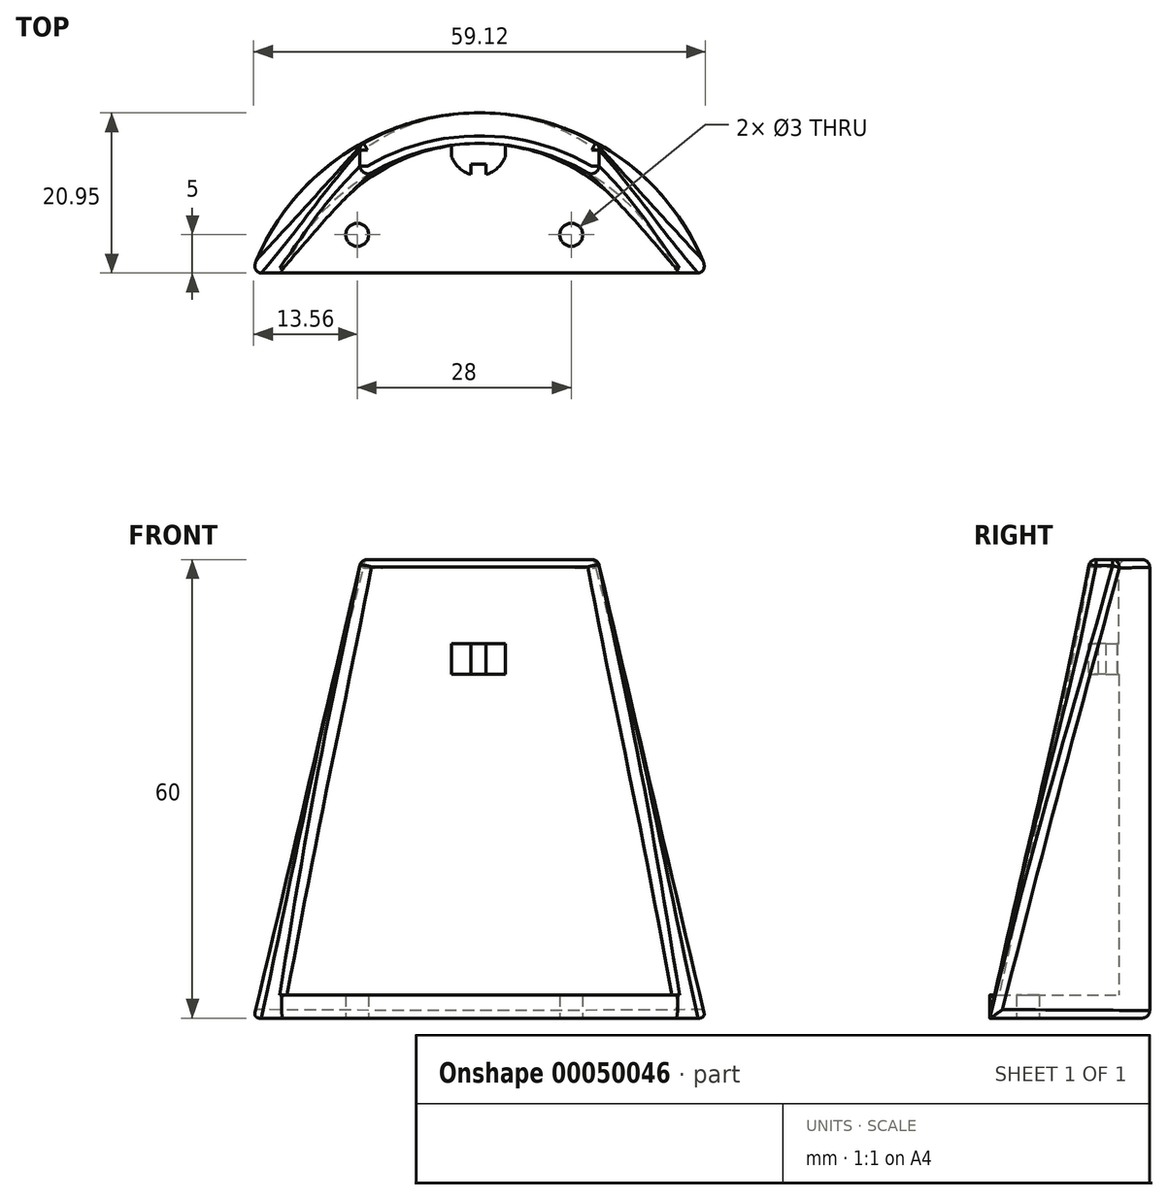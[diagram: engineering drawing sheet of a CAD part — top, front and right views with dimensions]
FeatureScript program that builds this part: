
annotation { "Feature Type Name" : "Feature", "Feature Type Description" : "" }
export const myFeature = defineFeature(function(context is Context, id is Id, definition is map)
    precondition{}
    {
        {
            var Q0;
            Q0=qCreatedBy(makeId("Top.planeOp"),FACE);
            var sketch = newSketch(context, id + "F0", { "sketchPlane" : qUnion([Q0])});
            skLineSegment(sketch, "E0.bottom", {"start": v(-24.17, 9.79) * mm, "end": v(35.83, 9.79) * mm, "construction": true});
            skLineSegment(sketch, "E0.top", {"start": v(-24.17, -15.21) * mm, "end": v(-20.17, -15.21) * mm});
            skLineSegment(sketch, "E0.left", {"start": v(-24.17, 9.79) * mm, "end": v(-24.17, -15.21) * mm, "construction": true});
            skLineSegment(sketch, "E0.right", {"start": v(35.83, 9.79) * mm, "end": v(35.83, -15.21) * mm, "construction": true});
            skArc(sketch, "E1", {"start": v(35.83, -15.21) * mm, "mid": v(5.83, 5.74) * mm, "end": v(-24.17, -15.21) * mm});
            skArc(sketch, "E2", {"start": v(31.83, -15.21) * mm, "mid": v(5.83, 1.74) * mm, "end": v(-20.17, -15.21) * mm});
            skLineSegment(sketch, "E3.trimOffspring", {"start": v(31.83, -15.21) * mm, "end": v(35.83, -15.21) * mm});
            skLineSegment(sketch, "E4", {"start": v(-20.17, -15.21) * mm, "end": v(31.83, -15.21) * mm});
            skCircle(sketch, "E5", {"center": v(-10.17, -10.21) * mm, "radius": 1.5 * mm});
            skCircle(sketch, "E6", {"center": v(17.83, -10.21) * mm, "radius": 1.5 * mm});
            skSolve(sketch);
        }
        {
            var Q0;
            Q0=qCreatedBy(makeId("Top.planeOp"),FACE);
            cPlane(context, id + "F1", {"entities" : qUnion([Q0]), "cplaneType" : CPlaneType.OFFSET, "offset" : 60 * mm, "width" : 150 * mm, "height" : 150 * mm});
        }
        {
            var Q0;
            Q0=qCreatedBy(id+"F1.planeOp",FACE);
            var sketch = newSketch(context, id + "F2", { "sketchPlane" : qUnion([Q0])});
            skArc(sketch, "E7", {"start": v(21.31, -2.84) * mm, "mid": v(5.83, 1.74) * mm, "end": v(-9.65, -2.84) * mm});
            skArc(sketch, "E8", {"start": v(21.31, 1.74) * mm, "mid": v(5.83, 5.74) * mm, "end": v(-9.65, 1.74) * mm});
            skPoint(sketch, "E8.startSnap0", {"position": v(5.83, 1.74) * mm});
            skPoint(sketch, "E8.endSnap0", {"position": v(5.83, 1.74) * mm});
            skLineSegment(sketch, "E9", {"start": v(-9.65, 1.74) * mm, "end": v(-9.65, -2.84) * mm});
            skLineSegment(sketch, "E10", {"start": v(21.31, 1.74) * mm, "end": v(21.31, -2.84) * mm});
            skSolve(sketch);
        }
        {
            var Q0;
            Q0=makeQuery(id+"F0.imprint","IMPRINT",FACE,{"disambiguationData":[TD([[makeQuery(id+"F0.imprint","IMPRINT",EDGE,{"derivedFrom":sQuery(id+"F0.wireOp",EDGE,"E0.top")}),1.0]])]});
            var Q1;
            Q1=makeQuery(id+"F2.imprint","IMPRINT",FACE,{"disambiguationData":[TD([[makeQuery(id+"F2.imprint","IMPRINT",EDGE,{"derivedFrom":sQuery(id+"F2.wireOp",EDGE,"E7")}),-1.0]])]});
            loft(context, id + "F3", {"sheetProfilesArray" : [{ "sheetProfileEntities" : qUnion([Q0]) }, { "sheetProfileEntities" : qUnion([Q1]) }]});
        }
        {
            var Q0;
            Q0=makeQuery(id+"F0.imprint","IMPRINT",FACE,{"disambiguationData":[TD([[makeQuery(id+"F0.imprint","IMPRINT",EDGE,{"derivedFrom":sQuery(id+"F0.wireOp",EDGE,"E2")}),1.0]])]});
            extrude(context, id + "F4", {"entities" : qUnion([Q0]), "operationType" : NewBodyOperationType.ADD, "depth" : 3 * mm});
        }
        {
            var Q0;
            Q0=makeQuery(id+"F4.opExtrude","SWEPT_EDGE",EDGE,{"disambiguationData":[OSD([sQuery(id+"F0.wireOp",EDGE,"E0.top"),sQuery(id+"F0.wireOp",EDGE,"E2"),sQuery(id+"F0.wireOp",EDGE,"E4")])]});
            var Q1;
            Q1=makeQuery(id+"F4.opExtrude","SWEPT_EDGE",EDGE,{"disambiguationData":[OSD([sQuery(id+"F0.wireOp",EDGE,"E2"),sQuery(id+"F0.wireOp",EDGE,"E3.trimOffspring"),sQuery(id+"F0.wireOp",EDGE,"E4")])]});
            var Q2;
            {var subQ0=sQuery(id+"F0.wireOp",EDGE,"E2");var subQ1=sQuery(id+"F0.wireOp",EDGE,"E4");Q2=makeQuery(id+"F4.boolean.opBoolean","SPLIT",EDGE,{"disambiguationData":[TD([makeQuery(id+"F3.opLoft","SWEPT_FACE",FACE,{"disambiguationData":[OSD([sQuery(id+"F0.wireOp",EDGE,"E1"),subQ0,sQuery(id+"F0.wireOp",EDGE,"E3.trimOffspring"),subQ1,sQuery(id+"F2.wireOp",EDGE,"E7"),sQuery(id+"F2.wireOp",EDGE,"E8"),sQuery(id+"F2.wireOp",EDGE,"E10")])]})])],"derivedFrom":makeQuery(id+"F4.opExtrude","CAP_EDGE",EDGE,{"disambiguationData":[OSD([subQ0])],"isStart":false})});}
            var Q3;
            {var subQ0=sQuery(id+"F0.wireOp",EDGE,"E2");var subQ1=sQuery(id+"F0.wireOp",EDGE,"E4");Q3=makeQuery(id+"F4.boolean.opBoolean","SPLIT",EDGE,{"disambiguationData":[TD([makeQuery(id+"F3.opLoft","SWEPT_FACE",FACE,{"disambiguationData":[OSD([sQuery(id+"F0.wireOp",EDGE,"E0.top"),sQuery(id+"F0.wireOp",EDGE,"E1"),subQ0,subQ1,sQuery(id+"F2.wireOp",EDGE,"E7"),sQuery(id+"F2.wireOp",EDGE,"E8"),sQuery(id+"F2.wireOp",EDGE,"E9")])]})])],"derivedFrom":makeQuery(id+"F4.opExtrude","CAP_EDGE",EDGE,{"disambiguationData":[OSD([subQ0])],"isStart":false})});}
            fillet(context, id + "F5", {"entities" : qUnion([Q0, Q1, Q2, Q3]), "radius" : .2 * mm, "tangentPropagation" : true, "allowEdgeOverflow" : false});
        }
        {
            var Q0;
            Q0=makeQuery(id+"F3.opLoft","SWEPT_EDGE",EDGE,{"disambiguationData":[OSD([sQuery(id+"F0.wireOp",EDGE,"E1"),sQuery(id+"F0.wireOp",EDGE,"E3.trimOffspring"),sQuery(id+"F2.wireOp",EDGE,"E8"),sQuery(id+"F2.wireOp",EDGE,"E10")])]});
            var Q1;
            Q1=makeQuery(id+"F3.opLoft","SWEPT_EDGE",EDGE,{"disambiguationData":[OSD([sQuery(id+"F0.wireOp",EDGE,"E2"),sQuery(id+"F0.wireOp",EDGE,"E3.trimOffspring"),sQuery(id+"F0.wireOp",EDGE,"E4"),sQuery(id+"F2.wireOp",EDGE,"E7"),sQuery(id+"F2.wireOp",EDGE,"E10")])]});
            var Q2;
            Q2=makeQuery(id+"F3.opLoft","MID_CAP_EDGE",EDGE,{"disambiguationData":[OSD([sQuery(id+"F2.wireOp",EDGE,"E7"),sQuery(id+"F2.wireOp",EDGE,"E8"),sQuery(id+"F2.wireOp",EDGE,"E10")])],"capPos":1.0});
            var Q3;
            Q3=makeQuery(id+"F3.opLoft","MID_CAP_EDGE",EDGE,{"disambiguationData":[OSD([sQuery(id+"F2.wireOp",EDGE,"E7"),sQuery(id+"F2.wireOp",EDGE,"E9"),sQuery(id+"F2.wireOp",EDGE,"E10")])],"capPos":1.0});
            var Q4;
            Q4=makeQuery(id+"F3.opLoft","MID_CAP_EDGE",EDGE,{"disambiguationData":[OSD([sQuery(id+"F2.wireOp",EDGE,"E8"),sQuery(id+"F2.wireOp",EDGE,"E9"),sQuery(id+"F2.wireOp",EDGE,"E10")])],"capPos":1.0});
            var Q5;
            Q5=makeQuery(id+"F3.opLoft","SWEPT_EDGE",EDGE,{"disambiguationData":[OSD([sQuery(id+"F0.wireOp",EDGE,"E0.top"),sQuery(id+"F0.wireOp",EDGE,"E2"),sQuery(id+"F0.wireOp",EDGE,"E4"),sQuery(id+"F2.wireOp",EDGE,"E7"),sQuery(id+"F2.wireOp",EDGE,"E9")])]});
            var Q6;
            Q6=makeQuery(id+"F3.opLoft","MID_CAP_EDGE",EDGE,{"disambiguationData":[OSD([sQuery(id+"F2.wireOp",EDGE,"E7"),sQuery(id+"F2.wireOp",EDGE,"E8"),sQuery(id+"F2.wireOp",EDGE,"E9")])],"capPos":1.0});
            var Q7;
            Q7=makeQuery(id+"F3.opLoft","SWEPT_EDGE",EDGE,{"disambiguationData":[OSD([sQuery(id+"F0.wireOp",EDGE,"E0.top"),sQuery(id+"F0.wireOp",EDGE,"E1"),sQuery(id+"F2.wireOp",EDGE,"E8"),sQuery(id+"F2.wireOp",EDGE,"E9")])]});
            var Q8;
            Q8=makeQuery(id+"F3.opLoft","MID_CAP_EDGE",EDGE,{"disambiguationData":[OSD([sQuery(id+"F0.wireOp",EDGE,"E0.top"),sQuery(id+"F0.wireOp",EDGE,"E1"),sQuery(id+"F0.wireOp",EDGE,"E3.trimOffspring")])],"capPos":0.0});
            fillet(context, id + "F6", {"entities" : qUnion([Q0, Q1, Q2, Q3, Q4, Q5, Q6, Q7, Q8]), "radius" : 1 * mm, "tangentPropagation" : true, "allowEdgeOverflow" : false});
        }
        {
            var Q0;
            Q0=qCreatedBy(makeId("Top.planeOp"),FACE);
            cPlane(context, id + "F7", {"entities" : qUnion([Q0]), "cplaneType" : CPlaneType.OFFSET, "offset" : 45 * mm, "width" : 150 * mm, "height" : 150 * mm});
        }
        {
            var Q0;
            Q0=qCreatedBy(id+"F7.planeOp",FACE);
            var sketch = newSketch(context, id + "F8", { "sketchPlane" : qUnion([Q0])});
            skArc(sketch, "E11", {"start": v(2.18, 0) * mm, "mid": v(5.68, -2.43) * mm, "end": v(9.18, 0) * mm});
            skLineSegment(sketch, "E12.bottom", {"start": v(2.18, 0) * mm, "end": v(9.18, 0) * mm});
            skLineSegment(sketch, "E13.top", {"start": v(2.18, 3) * mm, "end": v(9.18, 3) * mm});
            skLineSegment(sketch, "E13.left", {"start": v(2.18, 0) * mm, "end": v(2.18, 3) * mm});
            skLineSegment(sketch, "E13.right", {"start": v(9.18, 0) * mm, "end": v(9.18, 3) * mm});
            skLineSegment(sketch, "E14.top", {"start": v(4.68, -1) * mm, "end": v(6.68, -1) * mm});
            skLineSegment(sketch, "E14.left", {"start": v(4.68, -2.3) * mm, "end": v(4.68, -1) * mm});
            skLineSegment(sketch, "E14.right", {"start": v(6.68, -2.3) * mm, "end": v(6.68, -1) * mm});
            skLineSegment(sketch, "E15", {"start": v(5.68, 3) * mm, "end": v(5.68, -1) * mm, "construction": true});
            skPoint(sketch, "E16.orphan", {"position": v(5.68, -2.3) * mm});
            skSolve(sketch);
        }
        {
            var Q0;
            Q0=makeQuery(id+"F8.imprint","IMPRINT",FACE,{"disambiguationData":[TD([[makeQuery(id+"F8.imprint","IMPRINT",EDGE,{"derivedFrom":sQuery(id+"F8.wireOp",EDGE,"E12.bottom")}),1.0]])]});
            var Q1;
            {var subQ0=sQuery(id+"F8.wireOp",EDGE,"E12.bottom");Q1=makeQuery(id+"F8.imprint","IMPRINT",FACE,{"disambiguationData":[TD([[makeQuery(id+"F8.imprint","IMPRINT",EDGE,{"derivedFrom":subQ0}),-1.0]])]});}
            extrude(context, id + "F9", {"entities" : qUnion([Q0, Q1]), "operationType" : NewBodyOperationType.ADD, "depth" : 4 * mm});
        }
    });
